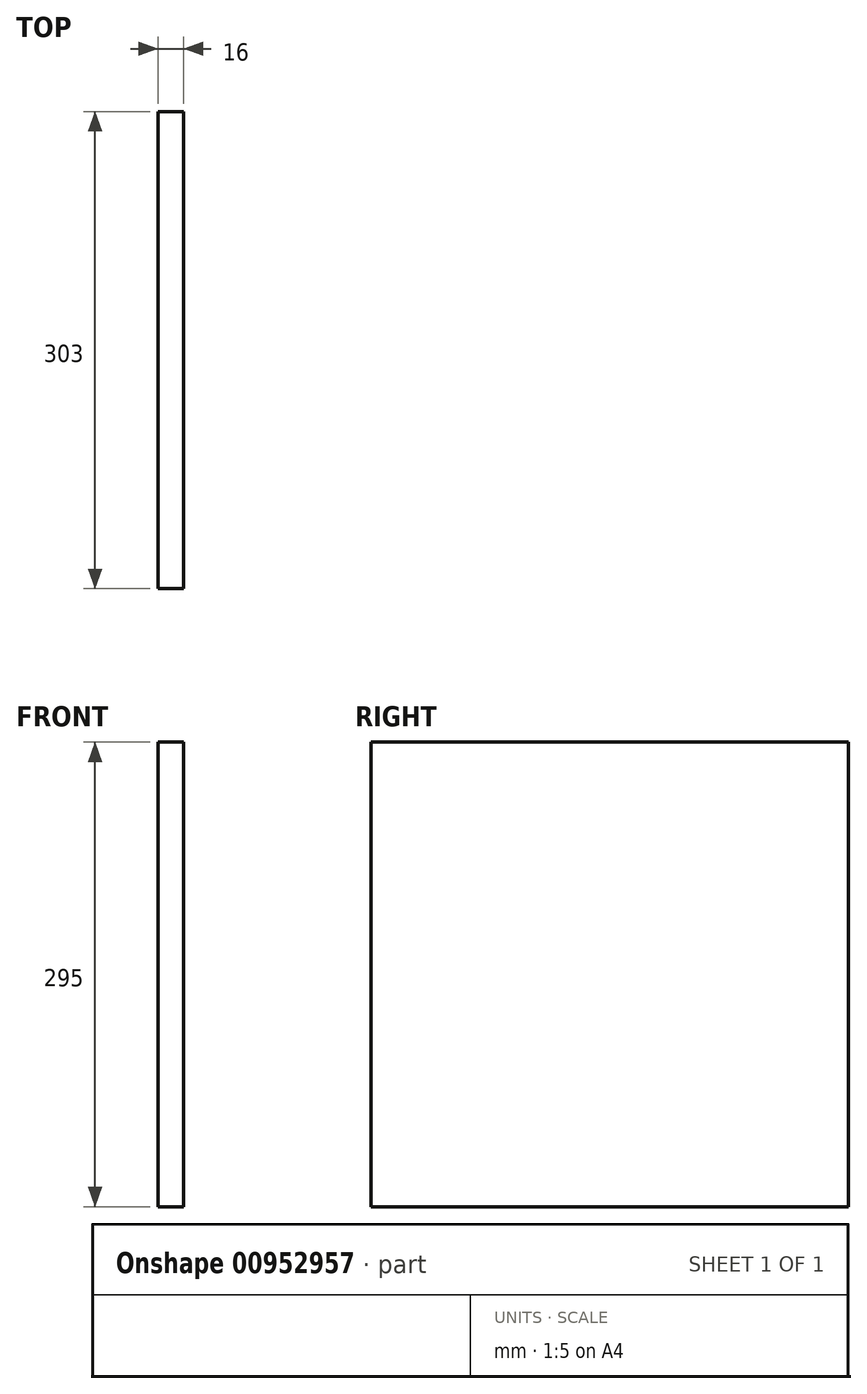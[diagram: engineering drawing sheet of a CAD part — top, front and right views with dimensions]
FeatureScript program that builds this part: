
annotation { "Feature Type Name" : "Feature", "Feature Type Description" : "" }
export const myFeature = defineFeature(function(context is Context, id is Id, definition is map)
    precondition{}
    {
        {
            var Q0;
            Q0=qCreatedBy(makeId("Right.planeOp"),FACE);
            var sketch = newSketch(context, id + "F0", { "sketchPlane" : qUnion([Q0])});
            skLineSegment(sketch, "E0.bottom", {"start": v(-172.8, 138.72) * mm, "end": v(130.2, 138.72) * mm});
            skLineSegment(sketch, "E0.top", {"start": v(-172.8, -156.28) * mm, "end": v(130.2, -156.28) * mm});
            skLineSegment(sketch, "E0.left", {"start": v(-172.8, 138.72) * mm, "end": v(-172.8, -156.28) * mm});
            skLineSegment(sketch, "E0.right", {"start": v(130.2, 138.72) * mm, "end": v(130.2, -156.28) * mm});
            skSolve(sketch);
        }
        {
            var Q0;
            Q0=qSketchRegion(id+"F0",true);
            extrude(context, id + "F1", {"entities" : qUnion([Q0]), "depth" : 16 * mm, "offsetDistance" : 25 * mm});
        }
    });
